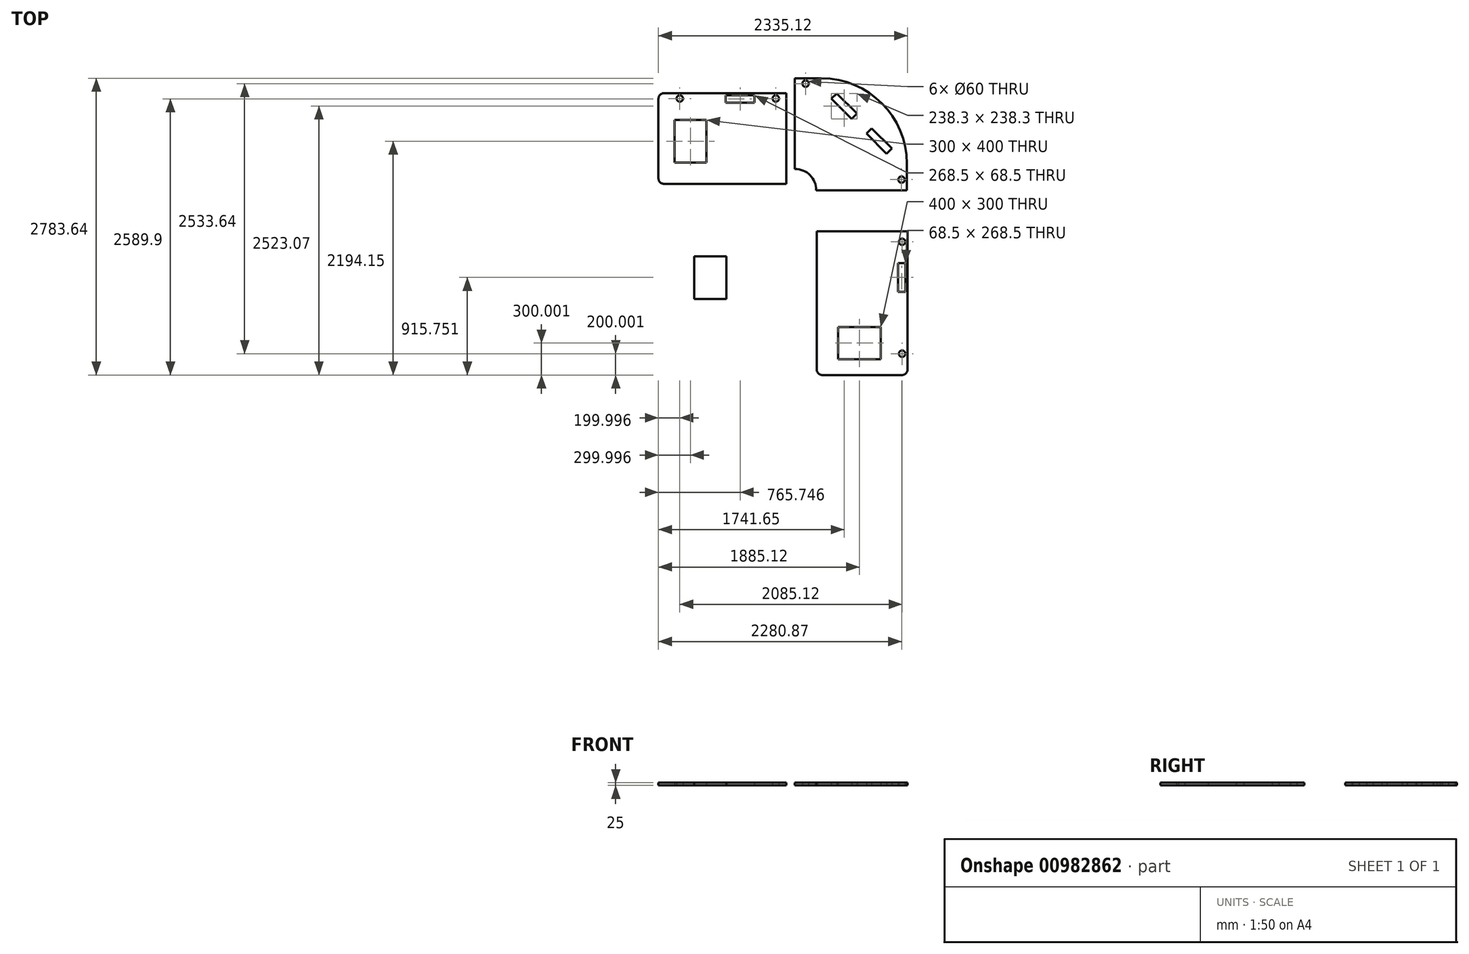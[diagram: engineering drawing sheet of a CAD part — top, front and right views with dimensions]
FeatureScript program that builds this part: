
annotation { "Feature Type Name" : "Feature", "Feature Type Description" : "" }
export const myFeature = defineFeature(function(context is Context, id is Id, definition is map)
    precondition{}
    {
        {
            var Q0;
            Q0=qCreatedBy(makeId("Top.planeOp"),FACE);
            var sketch = newSketch(context, id + "F0", { "sketchPlane" : qUnion([Q0])});
            skLineSegment(sketch, "E0.bottom", {"start": v(-1113.53, 803.85) * mm, "end": v(36.47, 803.85) * mm});
            skLineSegment(sketch, "E0.top", {"start": v(-1113.53, -46.15) * mm, "end": v(36.47, -46.15) * mm});
            skLineSegment(sketch, "E0.left", {"start": v(-1163.53, 753.85) * mm, "end": v(-1163.53, 3.85) * mm});
            skLineSegment(sketch, "E0.right", {"start": v(36.47, 803.85) * mm, "end": v(36.47, -46.15) * mm});
            skLineSegment(sketch, "E1.bottom", {"start": v(116, 943.34) * mm, "end": v(366, 943.34) * mm});
            skLineSegment(sketch, "E1.right", {"start": v(1166, 143.34) * mm, "end": v(1166, -106.66) * mm});
            skLineSegment(sketch, "E2", {"start": v(365.9, -106.66) * mm, "end": v(1166, -106.66) * mm});
            skLineSegment(sketch, "E3", {"start": v(116, 93.34) * mm, "end": v(116, 943.34) * mm});
            skLineSegment(sketch, "E4.bottom", {"start": v(321.59, -490.3) * mm, "end": v(1171.59, -490.3) * mm});
            skLineSegment(sketch, "E4.top", {"start": v(371.59, -1840.3) * mm, "end": v(1121.59, -1840.3) * mm});
            skLineSegment(sketch, "E4.left", {"start": v(321.59, -490.3) * mm, "end": v(321.59, -1790.3) * mm});
            skLineSegment(sketch, "E4.right", {"start": v(1171.59, -490.3) * mm, "end": v(1171.59, -1790.3) * mm});
            skPoint(sketch, "E5.visualSharp", {"position": v(321.59, -1840.3) * mm});
            skArc(sketch, "E5.filletArc", {"start": v(321.59, -1790.3) * mm, "mid": v(336.23, -1825.65) * mm, "end": v(371.59, -1840.3) * mm});
            skPoint(sketch, "E6.visualSharp", {"position": v(1171.59, -1840.3) * mm});
            skArc(sketch, "E6.filletArc", {"start": v(1121.59, -1840.3) * mm, "mid": v(1156.94, -1825.65) * mm, "end": v(1171.59, -1790.3) * mm});
            skPoint(sketch, "E7.visualSharp", {"position": v(-1163.53, -46.15) * mm});
            skArc(sketch, "E7.filletArc", {"start": v(-1163.53, 3.85) * mm, "mid": v(-1148.89, -31.5) * mm, "end": v(-1113.53, -46.15) * mm});
            skPoint(sketch, "E8.visualSharp", {"position": v(-1163.53, 803.85) * mm});
            skArc(sketch, "E8.filletArc", {"start": v(-1113.53, 803.85) * mm, "mid": v(-1148.89, 789.2) * mm, "end": v(-1163.53, 753.85) * mm});
            skPoint(sketch, "E9.visualSharp", {"position": v(1166, 943.34) * mm});
            skArc(sketch, "E9.filletArc", {"start": v(1166, 143.34) * mm, "mid": v(931.68, 709.03) * mm, "end": v(366, 943.34) * mm});
            skLineSegment(sketch, "E10.bottom", {"start": v(-1013.53, 553.85) * mm, "end": v(-713.53, 553.85) * mm});
            skLineSegment(sketch, "E10.top", {"start": v(-1013.53, 153.85) * mm, "end": v(-713.53, 153.85) * mm});
            skLineSegment(sketch, "E10.left", {"start": v(-1013.53, 553.85) * mm, "end": v(-1013.53, 153.85) * mm});
            skLineSegment(sketch, "E10.right", {"start": v(-713.53, 553.85) * mm, "end": v(-713.53, 153.85) * mm});
            skLineSegment(sketch, "E11.bottom", {"start": v(521.59, -1690.3) * mm, "end": v(921.59, -1690.3) * mm});
            skLineSegment(sketch, "E11.top", {"start": v(521.59, -1390.3) * mm, "end": v(921.59, -1390.3) * mm});
            skLineSegment(sketch, "E11.left", {"start": v(521.59, -1690.3) * mm, "end": v(521.59, -1390.3) * mm});
            skLineSegment(sketch, "E11.right", {"start": v(921.59, -1690.3) * mm, "end": v(921.59, -1390.3) * mm});
            skLineSegment(sketch, "E12.bottom", {"start": v(-527.23, -1127.54) * mm, "end": v(-827.23, -1127.54) * mm});
            skLineSegment(sketch, "E12.top", {"start": v(-527.23, -727.54) * mm, "end": v(-827.23, -727.54) * mm});
            skLineSegment(sketch, "E12.left", {"start": v(-527.23, -1127.54) * mm, "end": v(-527.23, -727.54) * mm});
            skLineSegment(sketch, "E12.right", {"start": v(-827.23, -1127.54) * mm, "end": v(-827.23, -727.54) * mm});
            skArc(sketch, "E13", {"start": v(116, 93.34) * mm, "mid": v(257.41, 34.76) * mm, "end": v(316, -106.66) * mm});
            skLineSegment(sketch, "E14", {"start": v(365.9, -106.66) * mm, "end": v(316, -106.66) * mm});
            skLineSegment(sketch, "E15", {"start": v(36.47, 703.85) * mm, "end": v(-1163.53, 703.85) * mm});
            skLineSegment(sketch, "E16", {"start": v(1071.59, -490.3) * mm, "end": v(1071.59, -1840.3) * mm});
            skLineSegment(sketch, "E17", {"start": v(366, 943.34) * mm, "end": v(366, 843.34) * mm});
            skLineSegment(sketch, "E18", {"start": v(366, 843.34) * mm, "end": v(116, 843.34) * mm});
            skLineSegment(sketch, "E19", {"start": v(1166, 143.34) * mm, "end": v(1066, 143.34) * mm});
            skLineSegment(sketch, "E20", {"start": v(1066, 143.34) * mm, "end": v(1066, -106.66) * mm});
            skArc(sketch, "E21", {"start": v(1066, 143.34) * mm, "mid": v(860.97, 638.32) * mm, "end": v(366, 843.34) * mm});
            skLineSegment(sketch, "E22", {"start": v(-1063.53, 803.85) * mm, "end": v(-1063.53, 703.85) * mm});
            skLineSegment(sketch, "E23", {"start": v(1171.59, -1740.3) * mm, "end": v(1071.59, -1740.3) * mm});
            skCircle(sketch, "E24", {"center": v(-963.53, 753.85) * mm, "radius": 30 * mm});
            skPoint(sketch, "E24.centerSnap0", {"position": v(-1063.53, 753.85) * mm});
            skCircle(sketch, "E25", {"center": v(-63.53, 753.85) * mm, "radius": 30 * mm});
            skLineSegment(sketch, "E26", {"start": v(-63.53, 753.85) * mm, "end": v(-63.53, 803.85) * mm});
            skLineSegment(sketch, "E27", {"start": v(-963.53, 753.85) * mm, "end": v(-963.53, 803.85) * mm});
            skCircle(sketch, "E28", {"center": v(216, 893.34) * mm, "radius": 30 * mm});
            skPoint(sketch, "E28.centerSnap0", {"position": v(366, 893.34) * mm});
            skLineSegment(sketch, "E29", {"start": v(216, 893.34) * mm, "end": v(216, 943.34) * mm});
            skCircle(sketch, "E30", {"center": v(1116, -6.66) * mm, "radius": 30 * mm});
            skLineSegment(sketch, "E31", {"start": v(1116, -6.66) * mm, "end": v(1166, -6.66) * mm});
            skCircle(sketch, "E32", {"center": v(1121.59, -590.3) * mm, "radius": 30 * mm});
            skLineSegment(sketch, "E33", {"start": v(1121.59, -590.3) * mm, "end": v(1171.59, -590.3) * mm});
            skCircle(sketch, "E34", {"center": v(1121.59, -1640.3) * mm, "radius": 30 * mm});
            skLineSegment(sketch, "E35", {"start": v(1121.59, -1640.3) * mm, "end": v(1171.59, -1640.3) * mm});
            skLineSegment(sketch, "E36", {"start": v(1121.59, -1640.3) * mm, "end": v(1121.59, -1740.3) * mm});
            skLineSegment(sketch, "E37", {"start": v(1121.59, -590.3) * mm, "end": v(1121.59, -490.3) * mm});
            skLineSegment(sketch, "E38", {"start": v(1116, -6.66) * mm, "end": v(1116, -106.66) * mm});
            skLineSegment(sketch, "E39", {"start": v(216, 893.34) * mm, "end": v(116, 893.34) * mm});
            skLineSegment(sketch, "E40", {"start": v(-63.53, 753.85) * mm, "end": v(36.47, 753.85) * mm});
            skLineSegment(sketch, "E41", {"start": v(-963.53, 753.85) * mm, "end": v(-1063.53, 753.85) * mm});
            skLineSegment(sketch, "E42.bottom", {"start": v(-532.03, 715.35) * mm, "end": v(-263.53, 715.35) * mm});
            skLineSegment(sketch, "E42.top", {"start": v(-532.03, 783.85) * mm, "end": v(-263.53, 783.85) * mm});
            skLineSegment(sketch, "E42.left", {"start": v(-532.03, 715.35) * mm, "end": v(-532.03, 783.85) * mm});
            skLineSegment(sketch, "E42.right", {"start": v(-263.53, 715.35) * mm, "end": v(-263.53, 783.85) * mm});
            skLineSegment(sketch, "E43.bottom", {"start": v(1083.09, -790.3) * mm, "end": v(1151.59, -790.3) * mm});
            skLineSegment(sketch, "E43.top", {"start": v(1083.09, -1058.8) * mm, "end": v(1151.59, -1058.8) * mm});
            skLineSegment(sketch, "E43.left", {"start": v(1083.09, -790.3) * mm, "end": v(1083.09, -1058.8) * mm});
            skLineSegment(sketch, "E43.right", {"start": v(1151.59, -790.3) * mm, "end": v(1151.59, -1058.8) * mm});
            skLineSegment(sketch, "E44", {"start": v(366, 943.34) * mm, "end": v(1166, 143.34) * mm});
            skLineSegment(sketch, "E45", {"start": v(1166, 143.34) * mm, "end": v(1024.57, 284.76) * mm});
            skLineSegment(sketch, "E46", {"start": v(1024.57, 284.76) * mm, "end": v(976.13, 236.33) * mm});
            skLineSegment(sketch, "E47", {"start": v(976.13, 236.33) * mm, "end": v(786.28, 426.18) * mm});
            skLineSegment(sketch, "E48", {"start": v(786.28, 426.18) * mm, "end": v(834.71, 474.62) * mm});
            skLineSegment(sketch, "E49", {"start": v(366, 943.34) * mm, "end": v(507.41, 801.92) * mm});
            skLineSegment(sketch, "E50", {"start": v(507.41, 801.92) * mm, "end": v(458.98, 753.48) * mm});
            skLineSegment(sketch, "E51", {"start": v(458.98, 753.48) * mm, "end": v(648.84, 563.63) * mm});
            skLineSegment(sketch, "E52", {"start": v(648.84, 563.63) * mm, "end": v(697.27, 612.06) * mm});
            skSolve(sketch);
        }
        {
            var Q0;
            Q0 = qSketchRegion(id + "F0", true);
            var Q1;
            {var subQ0=sQuery(id+"F0.wireOp",EDGE,"E45");var subQ7=sQuery(id+"F0.wireOp",EDGE,"E21");var subQ8=makeQuery(id+"F0.imprint","INTERSECT",VERTEX,{"derivedFrom":[subQ7,subQ0]});Q1=makeQuery(id+"F0.imprint","IMPRINT",FACE,{"disambiguationData":[TD([[makeQuery(id+"F0.imprint","IMPRINT",EDGE,{"disambiguationData":[TD([[subQ8,-1.0]])],"derivedFrom":subQ7}),1.0]])]});}
            extrude(context, id + "F1", {"entities" : qUnion([Q0, Q1]), "depth" : 25 * mm, "offsetDistance" : 25 * mm});
        }
    });
